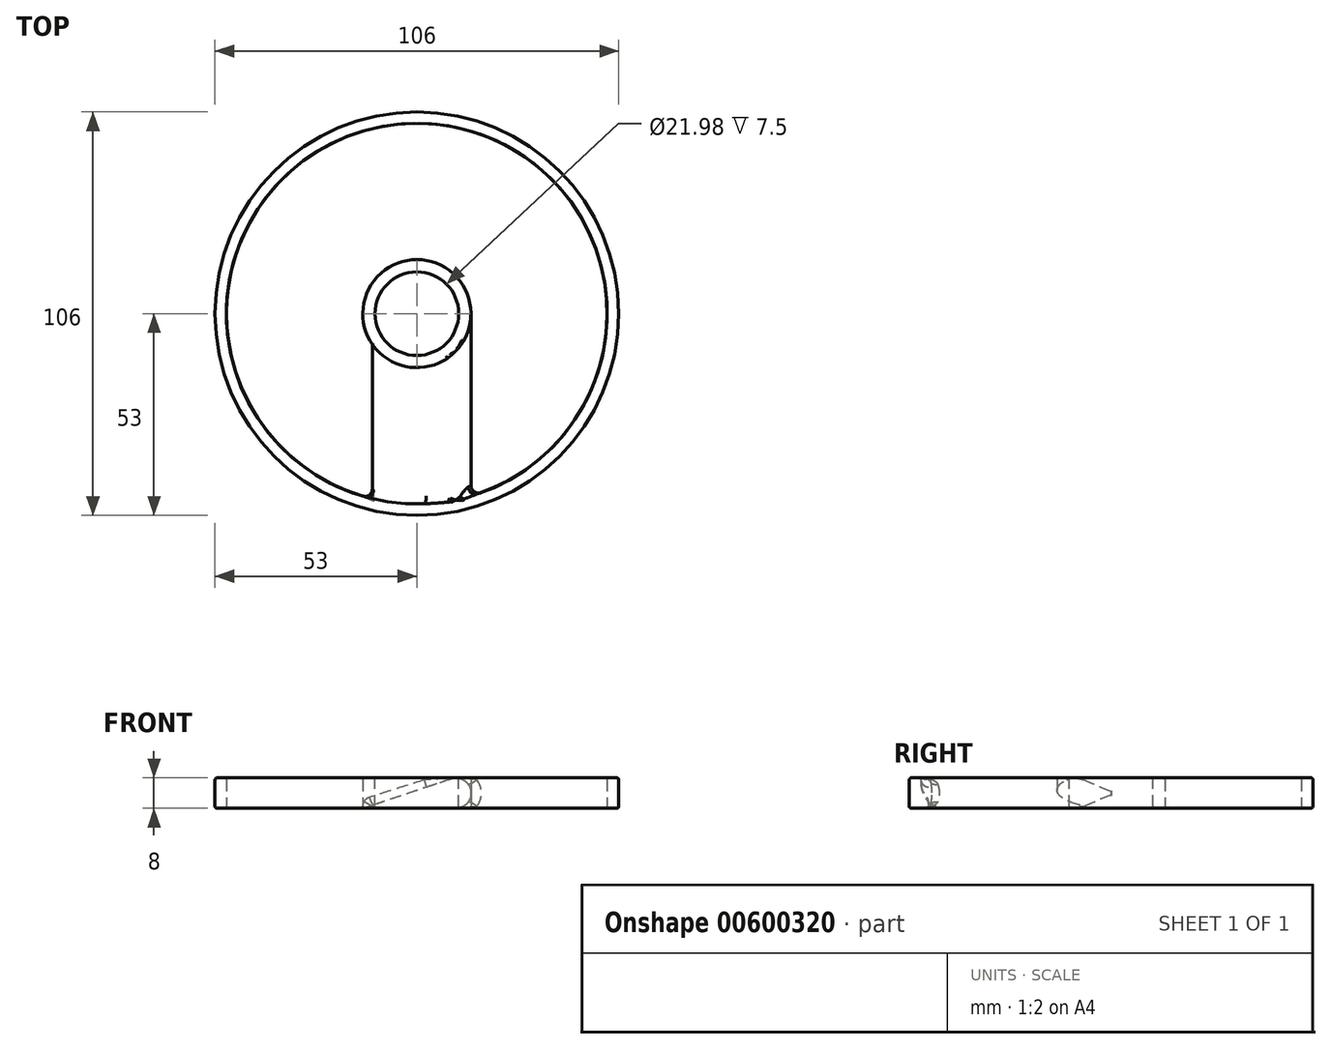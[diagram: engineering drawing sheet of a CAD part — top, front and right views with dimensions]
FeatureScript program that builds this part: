
annotation { "Feature Type Name" : "Feature", "Feature Type Description" : "" }
export const myFeature = defineFeature(function(context is Context, id is Id, definition is map)
    precondition{}
    {
        {
            var Q0;
            Q0=qCreatedBy(makeId("Front.planeOp"),FACE);
            var sketch = newSketch(context, id + "F0", { "sketchPlane" : qUnion([Q0])});
            skArc(sketch, "E0", {"start": v(10.25, -4) * mm, "mid": v(14.2, 0.64) * mm, "end": v(8.98, 3.8) * mm});
            skLineSegment(sketch, "E1", {"start": v(10.25, -4) * mm, "end": v(-14.25, -4) * mm});
            skLineSegment(sketch, "E2", {"start": v(-14.25, -4) * mm, "end": v(8.98, 3.8) * mm});
            skLineSegment(sketch, "E3", {"start": v(14.25, 3.63) * mm, "end": v(14.25, -3.33) * mm, "construction": true});
            skLineSegment(sketch, "E4", {"start": v(-14.25, -4) * mm, "end": v(-14.25, 0) * mm, "construction": true});
            skLineSegment(sketch, "E5", {"start": v(-14.25, 0) * mm, "end": v(14.25, 0) * mm, "construction": true});
            skLineSegment(sketch, "E6", {"start": v(0, 0) * mm, "end": v(0, 10.36) * mm, "construction": true});
            skSolve(sketch);
        }
        {
            var Q0;
            Q0 = qSketchRegion(id + "F0", true);
            extrude(context, id + "F1", {"entities" : qUnion([Q0]), "depth" : 50 * mm, "offsetDistance" : 25 * mm});
        }
        {
            var Q0;
            Q0=qCreatedBy(makeId("Top.planeOp"),FACE);
            var sketch = newSketch(context, id + "F2", { "sketchPlane" : qUnion([Q0])});
            skCircle(sketch, "E7", {"center": v(0, 0) * mm, "radius": 14.2 * mm});
            skCircle(sketch, "E8", {"center": v(0, 0) * mm, "radius": 50 * mm});
            skCircle(sketch, "E9", {"center": v(0, 0) * mm, "radius": 53 * mm});
            skSolve(sketch);
        }
        {
            var Q0;
            Q0 = qSketchRegion(id + "F2", true);
            var Q1;
            Q1=makeQuery(id+"F2.imprint","IMPRINT",FACE,{"disambiguationData":[TD([[makeQuery(id+"F2.imprint","IMPRINT",EDGE,{"derivedFrom":sQuery(id+"F2.wireOp",EDGE,"E7")}),1.0]])]});
            extrude(context, id + "F3", {"entities" : qUnion([Q0, Q1]), "operationType" : NewBodyOperationType.ADD, "endBound" : BoundingType.SYMMETRIC, "depth" : 8 * mm, "offsetDistance" : 25 * mm});
        }
        {
            var Q0;
            Q0=makeQuery(id+"F3.opExtrude","CAP_FACE",FACE,{"disambiguationData":[OSD([sQuery(id+"F2.wireOp",EDGE,"E7")])],"isStart":false});
            var sketch = newSketch(context, id + "F4", { "sketchPlane" : qUnion([Q0])});
            skCircle(sketch, "E10", {"center": v(0, 0) * mm, "radius": 11 * mm});
            skSolve(sketch);
        }
        {
            var Q0;
            Q0 = qSketchRegion(id + "F4", true);
            extrude(context, id + "F5", {"entities" : qUnion([Q0]), "operationType" : NewBodyOperationType.REMOVE, "endBound" : BoundingType.THROUGH_ALL, "oppositeDirection" : true, "depth" : 25 * mm, "offsetDistance" : 25 * mm});
        }
        {
            var Q0;
            {var subQ0=sQuery(id+"F0.wireOp",EDGE,"E1");Q0=makeQuery(id+"F3.boolean.opBoolean","MERGE",FACE,{"derivedFrom":[makeQuery(id+"F1.opExtrude","SWEPT_FACE",FACE,{"disambiguationData":[OSD([subQ0])]}),makeQuery(id+"FDegFlG9CZerSTg_1.1.F1.opExtrude","SWEPT_FACE",FACE,{"disambiguationData":[OSD([subQ0])]}),makeQuery(id+"FDegFlG9CZerSTg_1.2.F1.opExtrude","SWEPT_FACE",FACE,{"disambiguationData":[OSD([subQ0])]}),makeQuery(id+"FDegFlG9CZerSTg_1.3.F1.opExtrude","SWEPT_FACE",FACE,{"disambiguationData":[OSD([subQ0])]}),makeQuery(id+"F3.opExtrude","CAP_FACE",FACE,{"disambiguationData":[OSD([sQuery(id+"F2.wireOp",EDGE,"E7")])],"isStart":true}),makeQuery(id+"F3.opExtrude","CAP_FACE",FACE,{"disambiguationData":[OSD([sQuery(id+"F2.wireOp",EDGE,"E8"),sQuery(id+"F2.wireOp",EDGE,"E9")])],"isStart":true})]});}
            fillet(context, id + "F6", {"entities" : qUnion([Q0]), "radius" : .5 * mm, "tangentPropagation" : true, "allowEdgeOverflow" : false});
        }
        {
            var Q0;
            Q0=makeQuery(id+"F3.opExtrude","CAP_FACE",FACE,{"disambiguationData":[OSD([sQuery(id+"F2.wireOp",EDGE,"E8"),sQuery(id+"F2.wireOp",EDGE,"E9")])],"isStart":false});
            var Q1;
            Q1=makeQuery(id+"F5.boolean.opBoolean","COPY",EDGE,{"derivedFrom":makeQuery(id+"F5.opExtrude","CAP_EDGE",EDGE,{"disambiguationData":[OSD([sQuery(id+"F4.wireOp",EDGE,"E10")])],"isStart":true})});
            var Q2;
            {var subQ0=sQuery(id+"F0.wireOp",EDGE,"E0");var subQ1=sQuery(id+"F2.wireOp",EDGE,"E7");Q2=makeQuery(id+"F3.boolean.opBoolean","SPLIT",EDGE,{"disambiguationData":[TD([makeQuery(id+"FDegFlG9CZerSTg_1.1.F1.opExtrude","SWEPT_FACE",FACE,{"disambiguationData":[OSD([subQ0])]}),makeQuery(id+"FDegFlG9CZerSTg_1.2.F1.opExtrude","SWEPT_FACE",FACE,{"disambiguationData":[OSD([subQ0])]}),makeQuery(id+"F3.opExtrude","SWEPT_FACE",FACE,{"disambiguationData":[OSD([subQ1])]}),makeQuery(id+"F3.opExtrude","CAP_FACE",FACE,{"disambiguationData":[OSD([subQ1])],"isStart":false})])],"derivedFrom":makeQuery(id+"F3.opExtrude","CAP_EDGE",EDGE,{"disambiguationData":[OSD([subQ1])],"isStart":false})});}
            fillet(context, id + "F7", {"entities" : qUnion([Q0, Q1, Q2]), "radius" : .5 * mm, "tangentPropagation" : true, "allowEdgeOverflow" : false});
        }
        {
            var Q0;
            Q0=makeQuery(id+"F3.boolean.opBoolean","INTERSECT",EDGE,{"derivedFrom":[makeQuery(id+"FDegFlG9CZerSTg_1.1.F1.opExtrude","SWEPT_FACE",FACE,{"disambiguationData":[OSD([sQuery(id+"F0.wireOp",EDGE,"E2")])]}),makeQuery(id+"F3.opExtrude","SWEPT_FACE",FACE,{"disambiguationData":[OSD([sQuery(id+"F2.wireOp",EDGE,"E8")])]})]});
            var Q1;
            Q1=makeQuery(id+"F3.boolean.opBoolean","INTERSECT",EDGE,{"disambiguationData":[OD(0.0)],"derivedFrom":[makeQuery(id+"FDegFlG9CZerSTg_1.1.F1.opExtrude","SWEPT_FACE",FACE,{"disambiguationData":[OSD([sQuery(id+"F0.wireOp",EDGE,"E0")])]}),makeQuery(id+"F3.opExtrude","SWEPT_FACE",FACE,{"disambiguationData":[OSD([sQuery(id+"F2.wireOp",EDGE,"E8")])]})]});
            var Q2;
            Q2=makeQuery(id+"F3.boolean.opBoolean","INTERSECT",EDGE,{"disambiguationData":[OD(0.0)],"derivedFrom":[makeQuery(id+"FDegFlG9CZerSTg_1.3.F1.opExtrude","SWEPT_FACE",FACE,{"disambiguationData":[OSD([sQuery(id+"F0.wireOp",EDGE,"E0")])]}),makeQuery(id+"F3.opExtrude","SWEPT_FACE",FACE,{"disambiguationData":[OSD([sQuery(id+"F2.wireOp",EDGE,"E8")])]})]});
            var Q3;
            Q3=makeQuery(id+"F3.boolean.opBoolean","INTERSECT",EDGE,{"derivedFrom":[makeQuery(id+"FDegFlG9CZerSTg_1.3.F1.opExtrude","SWEPT_FACE",FACE,{"disambiguationData":[OSD([sQuery(id+"F0.wireOp",EDGE,"E2")])]}),makeQuery(id+"F3.opExtrude","SWEPT_FACE",FACE,{"disambiguationData":[OSD([sQuery(id+"F2.wireOp",EDGE,"E8")])]})]});
            var Q4;
            Q4=makeQuery(id+"F3.boolean.opBoolean","INTERSECT",EDGE,{"disambiguationData":[OD(0.0)],"derivedFrom":[makeQuery(id+"F1.opExtrude","SWEPT_FACE",FACE,{"disambiguationData":[OSD([sQuery(id+"F0.wireOp",EDGE,"E0")])]}),makeQuery(id+"F3.opExtrude","SWEPT_FACE",FACE,{"disambiguationData":[OSD([sQuery(id+"F2.wireOp",EDGE,"E8")])]})]});
            var Q5;
            Q5=makeQuery(id+"F3.boolean.opBoolean","INTERSECT",EDGE,{"derivedFrom":[makeQuery(id+"F1.opExtrude","SWEPT_FACE",FACE,{"disambiguationData":[OSD([sQuery(id+"F0.wireOp",EDGE,"E2")])]}),makeQuery(id+"F3.opExtrude","SWEPT_FACE",FACE,{"disambiguationData":[OSD([sQuery(id+"F2.wireOp",EDGE,"E8")])]})]});
            var Q6;
            Q6=makeQuery(id+"F3.boolean.opBoolean","INTERSECT",EDGE,{"disambiguationData":[OD(0.0)],"derivedFrom":[makeQuery(id+"FDegFlG9CZerSTg_1.2.F1.opExtrude","SWEPT_FACE",FACE,{"disambiguationData":[OSD([sQuery(id+"F0.wireOp",EDGE,"E0")])]}),makeQuery(id+"F3.opExtrude","SWEPT_FACE",FACE,{"disambiguationData":[OSD([sQuery(id+"F2.wireOp",EDGE,"E8")])]})]});
            var Q7;
            Q7=makeQuery(id+"F3.boolean.opBoolean","INTERSECT",EDGE,{"derivedFrom":[makeQuery(id+"FDegFlG9CZerSTg_1.2.F1.opExtrude","SWEPT_FACE",FACE,{"disambiguationData":[OSD([sQuery(id+"F0.wireOp",EDGE,"E2")])]}),makeQuery(id+"F3.opExtrude","SWEPT_FACE",FACE,{"disambiguationData":[OSD([sQuery(id+"F2.wireOp",EDGE,"E8")])]})]});
            fillet(context, id + "F8", {"entities" : qUnion([Q0, Q1, Q2, Q3, Q4, Q5, Q6, Q7]), "radius" : 2 * mm, "tangentPropagation" : true, "allowEdgeOverflow" : false});
        }
    });
